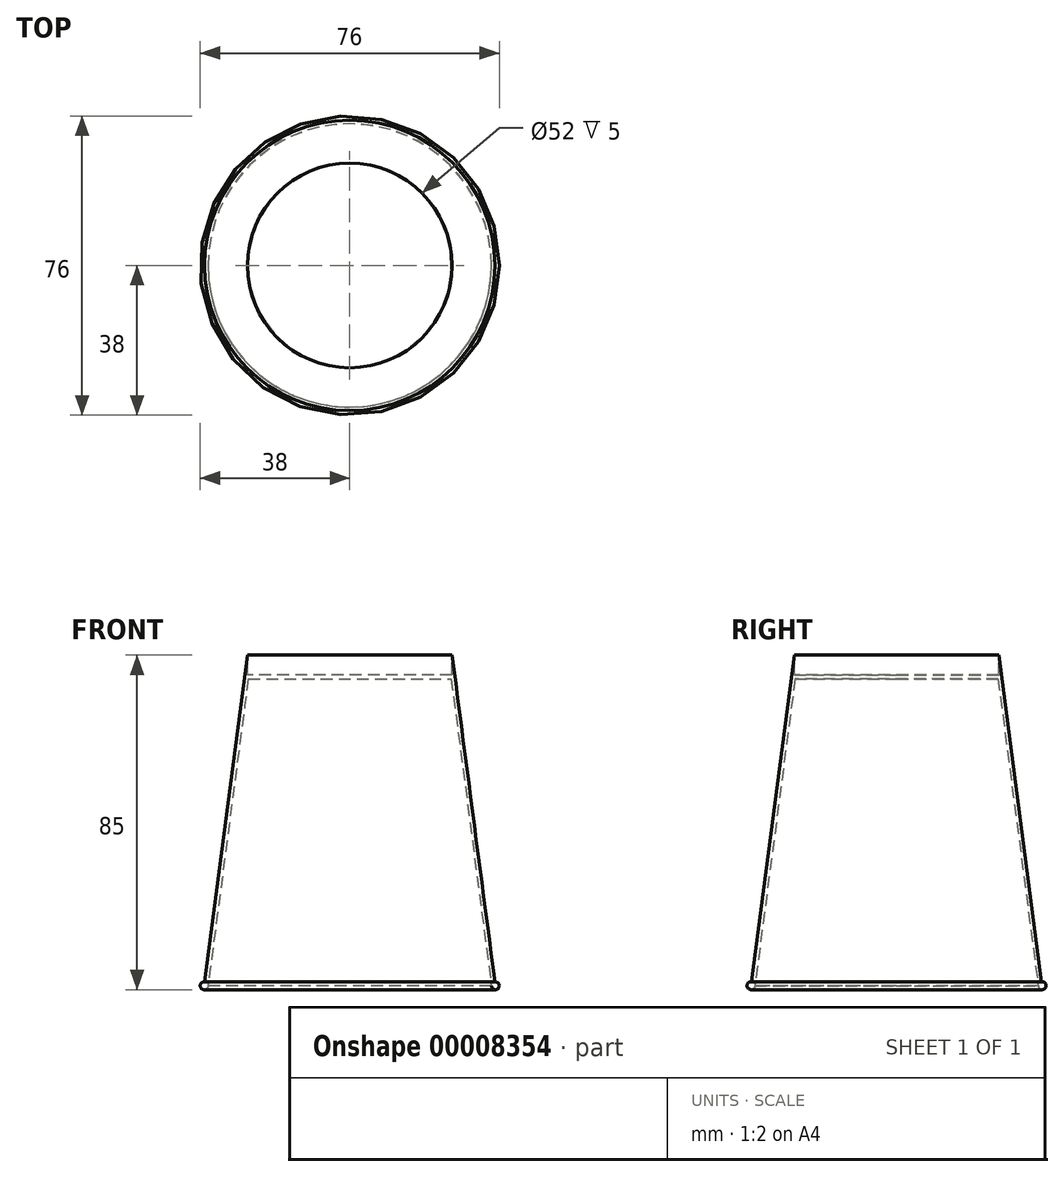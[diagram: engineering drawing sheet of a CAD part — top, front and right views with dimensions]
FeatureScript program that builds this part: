
annotation { "Feature Type Name" : "Feature", "Feature Type Description" : "" }
export const myFeature = defineFeature(function(context is Context, id is Id, definition is map)
    precondition{}
    {
        {
            var Q0;
            Q0=qCreatedBy(makeId("Front.planeOp"),FACE);
            var sketch = newSketch(context, id + "F0", { "sketchPlane" : qUnion([Q0])});
            skLineSegment(sketch, "E0", {"start": v(0, 0) * mm, "end": v(36, 0) * mm});
            skArc(sketch, "E1", {"start": v(36, 0) * mm, "mid": v(37.75, -0.66) * mm, "end": v(36.87, 1) * mm});
            skLineSegment(sketch, "E2", {"start": v(36.87, 1) * mm, "end": v(26, 84) * mm});
            skLineSegment(sketch, "E3", {"start": v(26, 84) * mm, "end": v(26, 79) * mm});
            skLineSegment(sketch, "E4", {"start": v(26, 79) * mm, "end": v(0, 79) * mm});
            skLineSegment(sketch, "E5", {"start": v(0, 79) * mm, "end": v(0, 0) * mm});
            skSolve(sketch);
        }
        {
            var Q0;
            Q0=makeQuery(id+"F0.imprint","IMPRINT",FACE,{"disambiguationData":[TD([[makeQuery(id+"F0.imprint","IMPRINT",EDGE,{"derivedFrom":sQuery(id+"F0.wireOp",EDGE,"E0")}),1.0]])]});
            var Q1;
            Q1=sQuery(id+"F0.wireOp",EDGE,"E5");
            revolve(context, id + "F1", {"entities" : qUnion([Q0]), "axis" : qUnion([Q1]), "revolveType" : RevolveType.FULL});
        }
        {
            var Q0;
            Q0=makeQuery(id+"F1.opRevolve","SWEPT_FACE",FACE,{"disambiguationData":[OSD([sQuery(id+"F0.wireOp",EDGE,"E0")])]});
            shell(context, id + "F2", {"entities" : qUnion([Q0]), "thickness" : 1 * mm});
        }
    });
